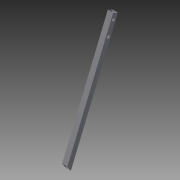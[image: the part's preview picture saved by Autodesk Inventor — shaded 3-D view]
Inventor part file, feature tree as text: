
AUTODESK INVENTOR PART (.ipt)
format: ipt  version: 2013 (Build 170138000, 138)  size: 106,496 bytes
history: native  units: in
note: dims shown in document units (in); Inventor stores cm internally (conversion verified against a paired STEP export)
features: extrude x3, sketch x3
ambient origin geometry x8: Origin, YZ Plane, XZ Plane, XY Plane, X Axis, Y Axis, Z Axis, Center Point
feature tree (6):
  extrude  "Extrusion3"  TaperAngle=90.0deg  [1 undecoded]
  extrude  "Extrusion4"  TaperAngle=22.5deg  [1 undecoded]
  extrude  "Extrusion5"  TaperAngle=180.0deg  [1 undecoded]
  sketch  "Sketch1"  dims[d0=10.0in d1=90.0deg]
  sketch  "Sketch3"  dims[d2=22.5in d3=22.5deg]
  sketch  "Sketch4"  dims[d4=1.0in d5=180.0deg d6=1.0in d7=112.5deg d8=90.0deg d17=1.0in d18=0.0in d19=0.0625in d20=0.0625in d21=0.0625in d22=0.0625in d23=100.0in d24=0.0in d25=1.0in d26=112.5deg d27=0.5in d28=2.5in d29=0.56in d30=2.0in d31=0.0in]
note: 3 required parameter values undecoded (feature->parameter linkage not recoverable at this tier; creation-order binding heuristic only, values carry confidence <= 0.55)
